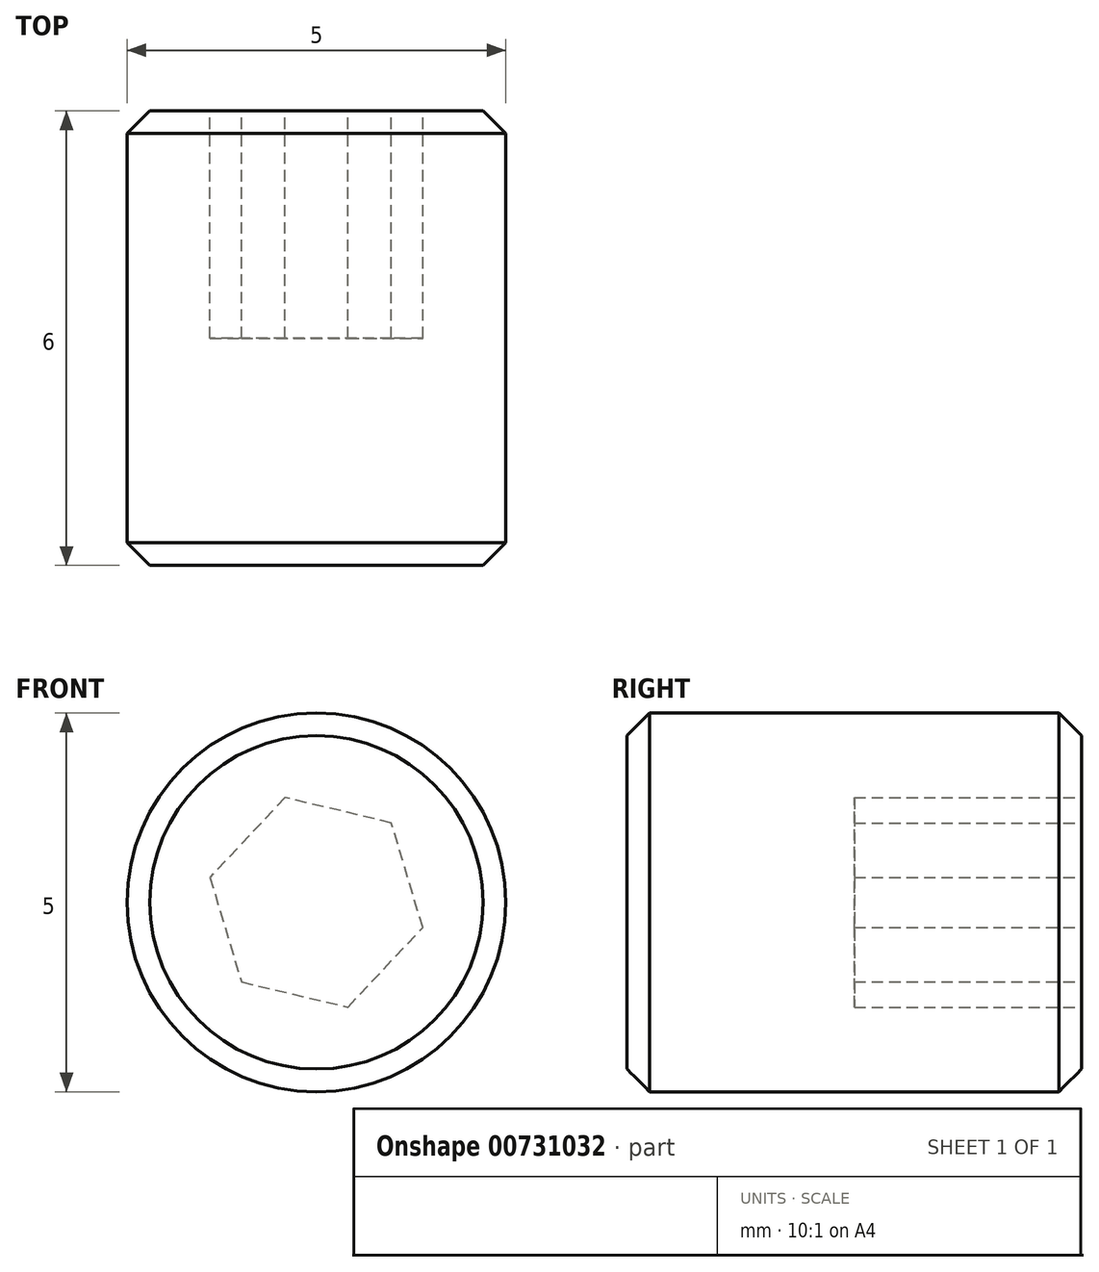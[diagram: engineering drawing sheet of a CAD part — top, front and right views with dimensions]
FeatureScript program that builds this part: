
annotation { "Feature Type Name" : "Feature", "Feature Type Description" : "" }
export const myFeature = defineFeature(function(context is Context, id is Id, definition is map)
    precondition{}
    {
        {
            var Q0;
            Q0=qCreatedBy(makeId("Front.planeOp"),FACE);
            var sketch = newSketch(context, id + "F0", { "sketchPlane" : qUnion([Q0])});
            skCircle(sketch, "E0", {"center": v(0, 0) * mm, "radius": 2.5 * mm});
            skSolve(sketch);
        }
        {
            var Q0;
            Q0=makeQuery(id+"F0.imprint","IMPRINT",FACE,{"disambiguationData":[TD([[makeQuery(id+"F0.imprint","IMPRINT",EDGE,{"derivedFrom":sQuery(id+"F0.wireOp",EDGE,"E0")}),1.0]])]});
            extrude(context, id + "F1", {"entities" : qUnion([Q0]), "depth" : 6 * mm, "offsetDistance" : 25 * mm});
        }
        {
            var Q0;
            Q0=makeQuery(id+"F1.opExtrude","CAP_EDGE",EDGE,{"disambiguationData":[OSD([sQuery(id+"F0.wireOp",EDGE,"E0")])],"isStart":false});
            var Q1;
            Q1=makeQuery(id+"F1.opExtrude","CAP_EDGE",EDGE,{"disambiguationData":[OSD([sQuery(id+"F0.wireOp",EDGE,"E0")])],"isStart":true});
            chamfer(context, id + "F2", {"entities" : qUnion([Q0, Q1]), "width" : 0.3 * mm, "tangentPropagation" : true});
        }
        {
            var Q0;
            Q0=makeQuery(id+"F1.opExtrude","CAP_FACE",FACE,{"disambiguationData":[OSD([sQuery(id+"F0.wireOp",EDGE,"E0")])],"isStart":true});
            var sketch = newSketch(context, id + "F3", { "sketchPlane" : qUnion([Q0])});
            skCircle(sketch, "E1.cCircle", {"center": v(0, 0) * mm, "radius": 1.25 * mm, "construction": true});
            skLineSegment(sketch, "E1.0", {"start": v(-1, 1.05) * mm, "end": v(0.41, 1.38) * mm});
            skLineSegment(sketch, "E1.1", {"start": v(0.41, 1.38) * mm, "end": v(1.4, 0.33) * mm});
            skLineSegment(sketch, "E1.2", {"start": v(1.4, 0.33) * mm, "end": v(1, -1.05) * mm});
            skLineSegment(sketch, "E1.3", {"start": v(1, -1.05) * mm, "end": v(-0.41, -1.38) * mm});
            skLineSegment(sketch, "E1.4", {"start": v(-0.41, -1.38) * mm, "end": v(-1.4, -0.33) * mm});
            skLineSegment(sketch, "E1.5", {"start": v(-1.4, -0.33) * mm, "end": v(-1, 1.05) * mm});
            skPoint(sketch, "E1.0.midPoint", {"position": v(-0.29, 1.22) * mm});
            skSolve(sketch);
        }
        {
            var Q0;
            Q0=makeQuery(id+"F3.imprint","IMPRINT",FACE,{"disambiguationData":[TD([[makeQuery(id+"F3.imprint","IMPRINT",EDGE,{"derivedFrom":sQuery(id+"F3.wireOp",EDGE,"E1.0")}),-1.0]])]});
            extrude(context, id + "F4", {"entities" : qUnion([Q0]), "operationType" : NewBodyOperationType.REMOVE, "oppositeDirection" : true, "depth" : 3 * mm, "offsetDistance" : 25 * mm});
        }
    });
